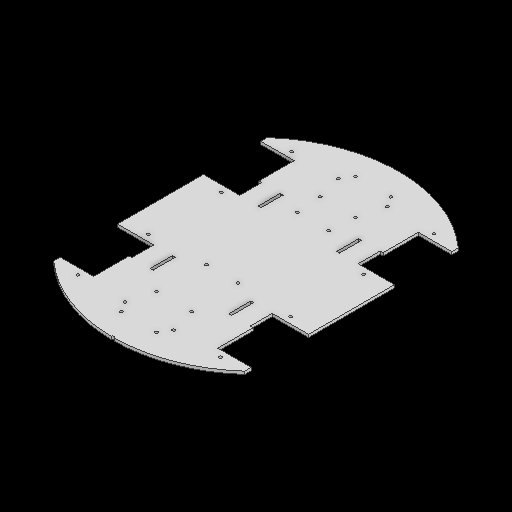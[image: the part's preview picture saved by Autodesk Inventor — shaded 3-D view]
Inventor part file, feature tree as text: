
AUTODESK INVENTOR PART (.ipt)
format: ipt  version: 2025.2 (Build 292293000, 293)  size: 180,736 bytes
history: native  units: in
note: dims shown in document units (in); Inventor stores cm internally (conversion verified against a paired STEP export)
features: extrude x1, sketch x1
ambient origin geometry x8: Origin, YZ Plane, XZ Plane, XY Plane, X Axis, Y Axis, Z Axis, Center Point
bodies: Solid1 (feature_tree)
feature tree (2):
  extrude  "Extrusion1"  [1 undecoded]
  sketch  "Sketch1"  dims[d0=0.1181in d1=0.0in]
note: 1 required parameter value undecoded (feature->parameter linkage not recoverable at this tier; creation-order binding heuristic only, values carry confidence <= 0.55)
